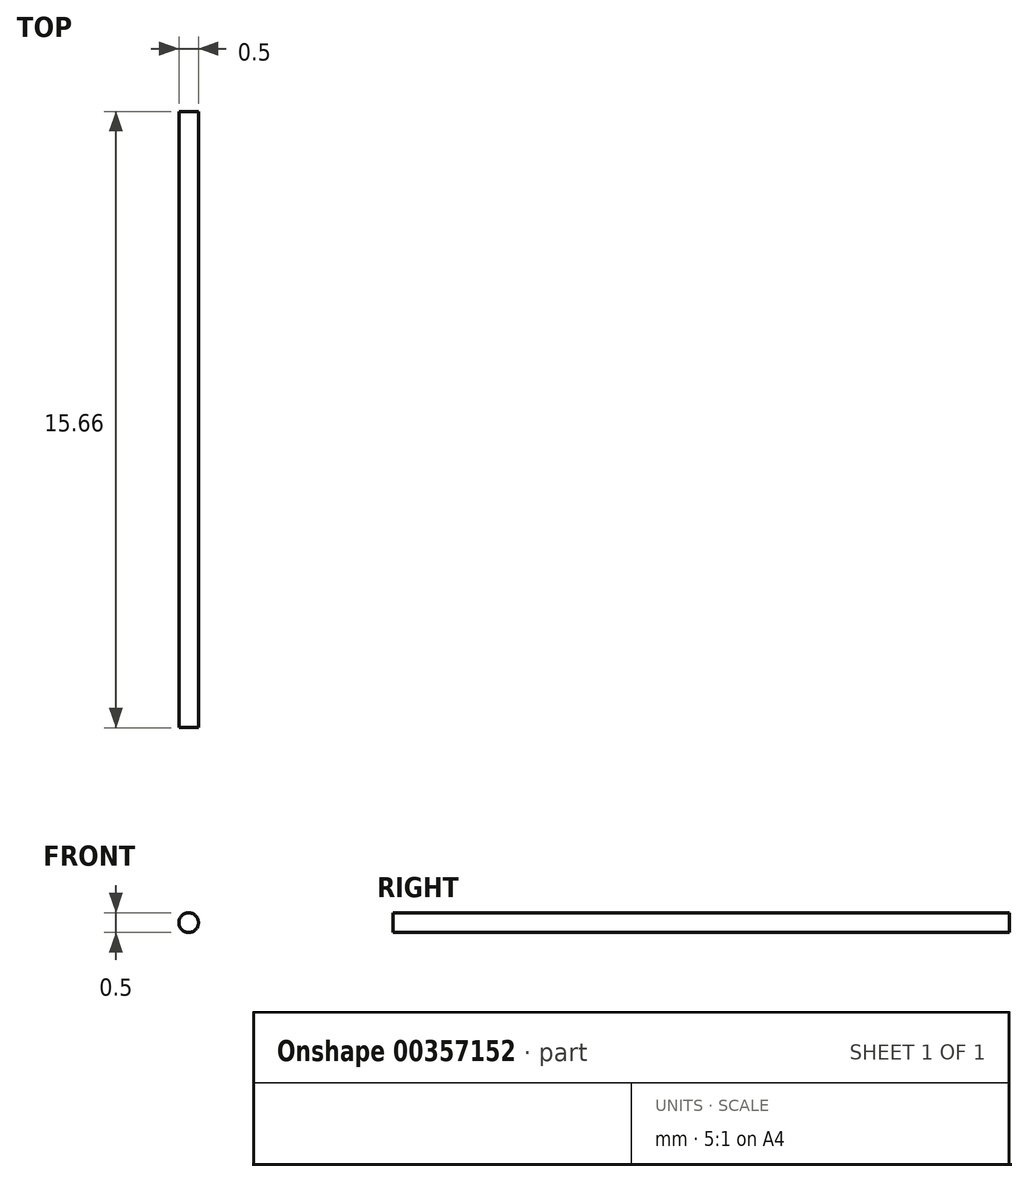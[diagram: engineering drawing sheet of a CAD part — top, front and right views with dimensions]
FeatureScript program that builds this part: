
annotation { "Feature Type Name" : "Feature", "Feature Type Description" : "" }
export const myFeature = defineFeature(function(context is Context, id is Id, definition is map)
    precondition{}
    {
        {
            var Q0;
            Q0=qCreatedBy(makeId("Front.planeOp"),FACE);
            var sketch = newSketch(context, id + "F0", { "sketchPlane" : qUnion([Q0])});
            skCircle(sketch, "E0", {"center": v(0, 0) * mm, "radius": 0.25 * mm});
            skSolve(sketch);
        }
        {
            var Q0;
            Q0=makeQuery(id+"F0.imprint","IMPRINT",FACE,{"disambiguationData":[TD([[makeQuery(id+"F0.imprint","IMPRINT",EDGE,{"derivedFrom":sQuery(id+"F0.wireOp",EDGE,"E0")}),1.0]])]});
            extrude(context, id + "F1", {"entities" : qUnion([Q0]), "endBound" : BoundingType.SYMMETRIC, "depth" : 15.65 * mm});
        }
    });
